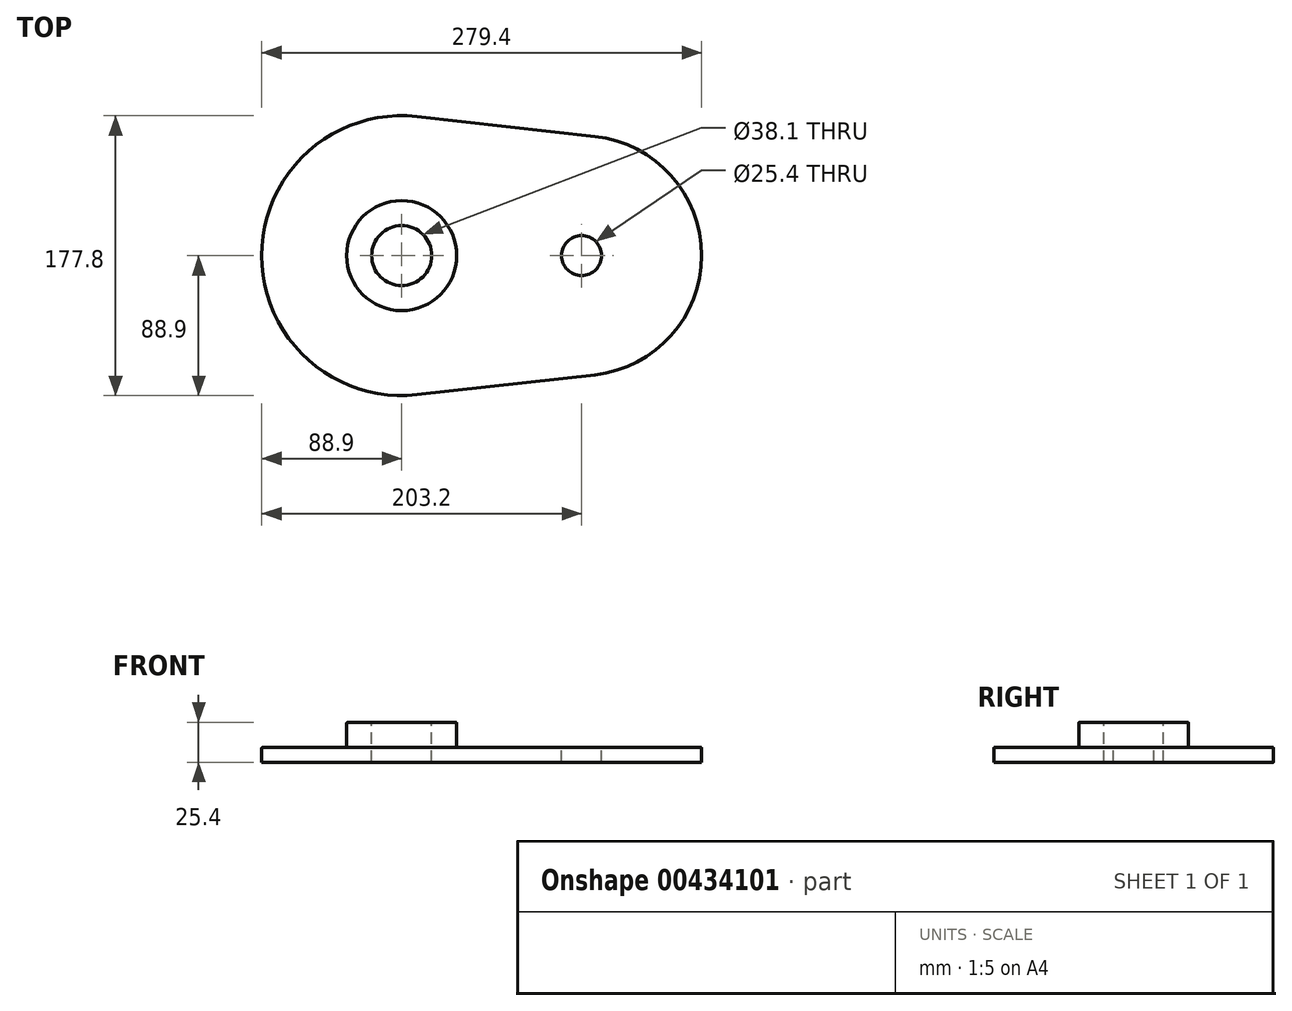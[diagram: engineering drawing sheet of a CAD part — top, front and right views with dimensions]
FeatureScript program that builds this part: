
annotation { "Feature Type Name" : "Feature", "Feature Type Description" : "" }
export const myFeature = defineFeature(function(context is Context, id is Id, definition is map)
    precondition{}
    {
        {
            var Q0;
            Q0=qCreatedBy(makeId("Top.planeOp"),FACE);
            var sketch = newSketch(context, id + "F0", { "sketchPlane" : qUnion([Q0])});
            skArc(sketch, "E0", {"start": v(9.88, 88.35) * mm, "mid": v(-88.9, 0) * mm, "end": v(9.88, -88.35) * mm});
            skArc(sketch, "E1", {"start": v(122.77, -75.73) * mm, "mid": v(190.5, 0) * mm, "end": v(122.77, 75.73) * mm});
            skLineSegment(sketch, "E2", {"start": v(9.88, 88.35) * mm, "end": v(122.77, 75.73) * mm});
            skLineSegment(sketch, "E3", {"start": v(9.88, -88.35) * mm, "end": v(122.77, -75.73) * mm});
            skLineSegment(sketch, "E4", {"start": v(0, 0) * mm, "end": v(224.72, 0) * mm, "construction": true});
            skPoint(sketch, "E4.endSnap0", {"position": v(190.5, 0) * mm});
            skSolve(sketch);
        }
        {
            var Q0;
            Q0=makeQuery(id+"F0.imprint","IMPRINT",FACE,{"disambiguationData":[TD([[makeQuery(id+"F0.imprint","IMPRINT",EDGE,{"derivedFrom":sQuery(id+"F0.wireOp",EDGE,"E0")}),1.0]])]});
            extrude(context, id + "F1", {"entities" : qUnion([Q0]), "depth" : 9.52 * mm});
        }
        {
            var Q0;
            Q0=makeQuery(id+"F1.opExtrude","CAP_FACE",FACE,{"disambiguationData":[OSD([sQuery(id+"F0.wireOp",EDGE,"E0"),sQuery(id+"F0.wireOp",EDGE,"E1"),sQuery(id+"F0.wireOp",EDGE,"E2"),sQuery(id+"F0.wireOp",EDGE,"E3")])],"isStart":false});
            var sketch = newSketch(context, id + "F2", { "sketchPlane" : qUnion([Q0])});
            skCircle(sketch, "E5", {"center": v(0, 0) * mm, "radius": 34.93 * mm});
            skSolve(sketch);
        }
        {
            var Q0;
            Q0 = qSketchRegion(id + "F2", true);
            var Q1;
            Q1=makeQuery(id+"F2.imprint","IMPRINT",FACE,{"disambiguationData":[TD([[makeQuery(id+"F2.imprint","IMPRINT",EDGE,{"derivedFrom":sQuery(id+"F2.wireOp",EDGE,"E5")}),1.0]])]});
            extrude(context, id + "F3", {"entities" : qUnion([Q0, Q1]), "operationType" : NewBodyOperationType.ADD, "depth" : 15.88 * mm});
        }
        {
            var Q0;
            Q0=makeQuery(id+"F3.opExtrude","CAP_FACE",FACE,{"disambiguationData":[OSD([sQuery(id+"F2.wireOp",EDGE,"E5")])],"isStart":false});
            var sketch = newSketch(context, id + "F4", { "sketchPlane" : qUnion([Q0])});
            skCircle(sketch, "E6", {"center": v(0, 0) * mm, "radius": 19.05 * mm});
            skCircle(sketch, "E7", {"center": v(114.3, 0) * mm, "radius": 12.7 * mm});
            skSolve(sketch);
        }
        {
            var Q0;
            Q0=makeQuery(id+"F4.imprint","IMPRINT",FACE,{"disambiguationData":[TD([[makeQuery(id+"F4.imprint","IMPRINT",EDGE,{"derivedFrom":sQuery(id+"F4.wireOp",EDGE,"E6")}),1.0]])]});
            var Q1;
            Q1=makeQuery(id+"F4.imprint","IMPRINT",FACE,{"disambiguationData":[TD([[makeQuery(id+"F4.imprint","IMPRINT",EDGE,{"derivedFrom":sQuery(id+"F4.wireOp",EDGE,"E7")}),1.0]])]});
            extrude(context, id + "F5", {"entities" : qUnion([Q0, Q1]), "operationType" : NewBodyOperationType.REMOVE, "endBound" : BoundingType.THROUGH_ALL, "oppositeDirection" : true, "depth" : 25.4 * mm});
        }
        {
            var Q0;
            Q0=makeQuery(id+"F3.opExtrude","CAP_EDGE",EDGE,{"disambiguationData":[OSD([sQuery(id+"F2.wireOp",EDGE,"E5")])],"isStart":true});
            var Q1;
            Q1=makeQuery(id+"F3.opExtrude","CAP_EDGE",EDGE,{"disambiguationData":[OSD([sQuery(id+"F2.wireOp",EDGE,"E5")])],"isStart":false});
            var Q2;
            Q2=makeQuery(id+"F1.opExtrude","CAP_EDGE",EDGE,{"disambiguationData":[OSD([sQuery(id+"F0.wireOp",EDGE,"E1")])],"isStart":false});
            var Q3;
            Q3=makeQuery(id+"F1.opExtrude","CAP_EDGE",EDGE,{"disambiguationData":[OSD([sQuery(id+"F0.wireOp",EDGE,"E3")])],"isStart":false});
            var Q4;
            Q4=makeQuery(id+"F1.opExtrude","CAP_FACE",FACE,{"disambiguationData":[OSD([sQuery(id+"F0.wireOp",EDGE,"E0"),sQuery(id+"F0.wireOp",EDGE,"E1"),sQuery(id+"F0.wireOp",EDGE,"E2"),sQuery(id+"F0.wireOp",EDGE,"E3")])],"isStart":false});
            fillet(context, id + "F6", {"entities" : qUnion([Q0, Q1, Q2, Q3, Q4]), "radius" : 0.8 * mm, "tangentPropagation" : true, "allowEdgeOverflow" : false});
        }
    });
